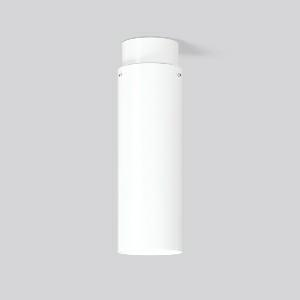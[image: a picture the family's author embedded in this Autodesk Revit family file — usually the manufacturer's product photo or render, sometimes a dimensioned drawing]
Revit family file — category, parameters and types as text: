
# Revit family: glasdownlight_931180_002_76_fa2b
name_source: partatom
category: Lighting Fixtures
units: mm (PartAtom-declared; Revit-internal decimal feet)

## family parameters
Cut with Voids When Loaded = No
Host = Face
Light Source = No
Part Type = Normal
Room Calculation Point = No
Round Connector Dimension = Use Diameter
Shared = No

## types (1)
- GLASDOWNLIGHT (1 x LED Modul 830, 3350 lm, 3000)
    Apparent Load = 26 VA
    CIE Flux Codes = 24 49 74 56 100
    Color Rendering = 80
    Color Temperature = 3000
    Default Elevation = 1800 mm
    Description = Series: GLASDOWNLIGHT
Decorative round surface-mounted luminaire. Base: aluminium, powder-coated. Mouth blown 3-layer opal glass (Triplex glass) with satin finish. Glass fastening: retaining screws. Triplex glass produces particularly homogeneous, soft and glare free lighting. 
Colour: white
Diameter: 150 mm
Height: 470 mm
Lamp: LED
Socket: without socket
Colour temperature: 3000K
Colour rendering index (CRI): 80
System power: 26 W
Rated luminous flux: 3350 lm
Luminous efficiency: 129 lm/W
Control gear: Converter, dimmable, DALI
Protection class: I
Type of protection: IP 20
    Height = 470 mm
    Lamp = 1 x LED Modul 830
    Lamp Light Flux = 3350 lm
    Lamp count = 1
    Length = 150 mm
    Lifetime = 50000 h
    Luminous efficacy = 129 lm/W
    Manufacturer = RZB
    ModVariant = No
    Model = 931180.002.76
    Mounting Place = Ceiling
    Mounting Type = Surface mounted
    Number of Poles = 1
    OnlyDefault = Yes
    Power Factor = 1
    Product Name = GLASDOWNLIGHT
    Product group = Surface mounted ceiling luminaires
    ProductGroupID = 303
    Protection Class = Protection class I
    Protection Degree = IP 20
    RLX_Detail_Level = 1
    RLX_Emergency_Light_Flux = 0 lm
    RLX_Emergency_Type = 0
    RLX_Emergency_Type_DB = No
    RlxData = <blob elided: 15521 chars, md5=795e8e44>
    Socket = socket
    Standby Power = 0 W
    System Light Flux = 3350 lm
    System Power = 26 W
    Type Comments = Product without accessories
    Type Image = 931180.002.jpg
    URL = http://relux.com
    VarID = ---
    Voltage = 230 V
    Voltage Range = 220-240 V
    Weight = 0.00 kg
    Width = 0 mm  [stored 0 ft]

note: [stored X ft] marks values corroborated as IEEE doubles in the binary element streams (Revit-internal decimal feet)

## geometry (parser evidence)
native form markers: Sweep x14
no freeform markers — native parametric forms only
